# Revit family: DBLTD_Kwickscreen_PrvcyScrnSym_Kin
name_source: partatom
category: Furniture
units: mm (PartAtom-declared; Revit-internal decimal feet)

## family parameters
Always vertical = Yes
Cut with Voids When Loaded = No
OmniClass Number = 23.40.20.00
OmniClass Title = General Furniture and Specialties
Room Calculation Point = No
Shared = No
Work Plane-Based = No

## types (1)
- Slim Fixed to the Wall Screen
    Assembly Code = E2020200
    AssetType = Movable
    BIMObjectName = Kwickscreen_PrvcyScrnSym_Kin
    Category = Pr_40_30_20_65:Privacy screens
    Color = Defined by material specified
    Cost = 0 $
    Description = Slim Fixed to the Wall Screen
    DurationUnit = Years
    ExpectedLife = 10
    Features = Kin is an unobtrusive fixed-to-wall screen, engineered for frequent use.
    Finish = Silver anodized Aluminium, but can be powder coated to any colour, and the printed inner panels can be printed with any design
    IfcExportAs = IfcFurnishingElementType
    IfcExportType = SCREEN
    Keynote = Pr_40_30_20_65
    MainColor = Defined by material specified
    Manufacturer = Kwickscreen
    ManufacturerName = Kwickscreen
    ManufacturerURL = https://kwickscreen.com
    Material = Extruded Aluminium body, Polyester film inner screen with nylon zips, Sheet metal bases and caps
    Model = Kin
    ModelNumber = Kin
    ModelReference = Slim Fixed to the Wall Screen
    NBSDescription = Privacy screen system
    NBSReference = 25-05-60/165
    Name = PrvcyScrnSym_Kwickscreen_Kin
    NominalHeight = 1900 mm  [stored 6.2336 ft]
    NominalLength = 2200 mm
    NominalWidth = 500 mm  [stored 1.64042 ft]
    ProductInformation = https://kwickscreen.com
    ReplacementCost = 0.00
    Size = W 500mm x D 150 - 2200mm x H 1900mm
    Type Comments = Slim Fixed to the Wall Screen
    URL = www.kwickscreen.com
    Uniclass2015Description = Privacy screens
    Uniclass2015Reference = Pr_40_30_20_65
    Uniclass2015Version = Products v1.3
    Version = 1
    WarrantyDescription = Our product quality and reliability is exceptionally high enabling us to provide a minimum 5 year warranty for normal use on all our products
    WarrantyDurationLabor = 5
    WarrantyDurationParts = 5
    WarrantyDurationUnit = Years

note: [stored X ft] marks values corroborated as IEEE doubles in the binary element streams (Revit-internal decimal feet)

## geometry (parser evidence)
native form markers: Revolve x2, Sweep x37
no freeform markers — native parametric forms only
